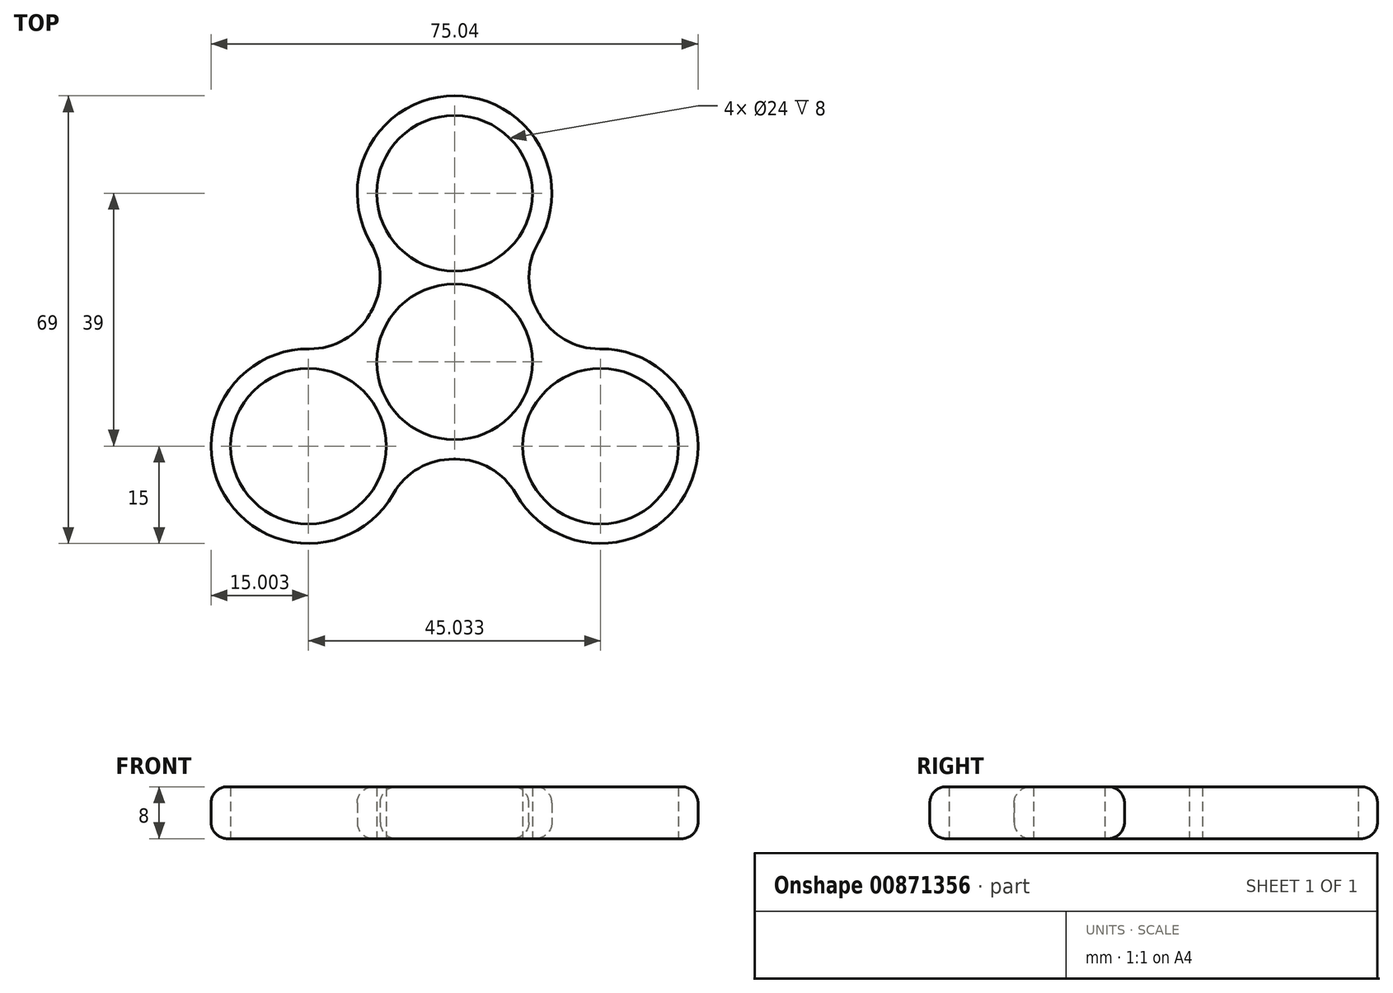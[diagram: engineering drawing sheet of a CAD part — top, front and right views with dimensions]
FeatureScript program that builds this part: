
annotation { "Feature Type Name" : "Feature", "Feature Type Description" : "" }
export const myFeature = defineFeature(function(context is Context, id is Id, definition is map)
    precondition{}
    {
        {
            var Q0;
            Q0=qCreatedBy(makeId("Top.planeOp"),FACE);
            var sketch = newSketch(context, id + "F0", { "sketchPlane" : qUnion([Q0])});
            skCircle(sketch, "E0", {"center": v(0, 0) * mm, "radius": 12 * mm});
            skCircle(sketch, "E1", {"center": v(0, 0) * mm, "radius": 26 * mm, "construction": true});
            skLineSegment(sketch, "E2", {"start": v(0, 0) * mm, "end": v(0, 26) * mm, "construction": true});
            skLineSegment(sketch, "E3", {"start": v(0, 0) * mm, "end": v(22.52, -13) * mm, "construction": true});
            skLineSegment(sketch, "E4", {"start": v(0, 0) * mm, "end": v(-22.52, -13) * mm, "construction": true});
            skCircle(sketch, "E5", {"center": v(0, 26) * mm, "radius": 12 * mm});
            skCircle(sketch, "E6", {"center": v(22.52, -13) * mm, "radius": 12 * mm});
            skCircle(sketch, "E7", {"center": v(-22.52, -13) * mm, "radius": 12 * mm});
            skCircle(sketch, "E8", {"center": v(0, 0) * mm, "radius": 41 * mm, "construction": true});
            skCircle(sketch, "E9", {"center": v(0, 26) * mm, "radius": 15 * mm});
            skCircle(sketch, "E10", {"center": v(-22.52, -13) * mm, "radius": 15 * mm});
            skCircle(sketch, "E11", {"center": v(22.52, -13) * mm, "radius": 15 * mm});
            skCircle(sketch, "E12", {"center": v(0, 0) * mm, "radius": 15 * mm});
            skSolve(sketch);
        }
        {
            var Q0;
            {var subQ0=sQuery(id+"F0.wireOp",EDGE,"E12");var subQ1=sQuery(id+"F0.wireOp",EDGE,"E5");var subQ2=makeQuery(id+"F0.imprint","INTERSECT",VERTEX,{"disambiguationData":[OD(0.0)],"derivedFrom":[subQ1,subQ0]});Q0=makeQuery(id+"F0.imprint","IMPRINT",FACE,{"disambiguationData":[TD([[makeQuery(id+"F0.imprint","IMPRINT",EDGE,{"disambiguationData":[TD([[subQ2,-1.0]])],"derivedFrom":subQ1}),-1.0]])]});}
            var Q1;
            {var subQ0=sQuery(id+"F0.wireOp",EDGE,"E9");var subQ1=sQuery(id+"F0.wireOp",EDGE,"E0");var subQ2=makeQuery(id+"F0.imprint","INTERSECT",VERTEX,{"disambiguationData":[OD(0.0)],"derivedFrom":[subQ1,subQ0]});Q1=makeQuery(id+"F0.imprint","IMPRINT",FACE,{"disambiguationData":[TD([[makeQuery(id+"F0.imprint","IMPRINT",EDGE,{"disambiguationData":[TD([[subQ2,-1.0]])],"derivedFrom":subQ1}),-1.0]])]});}
            var Q2;
            {var subQ0=sQuery(id+"F0.wireOp",EDGE,"E12");var subQ1=sQuery(id+"F0.wireOp",EDGE,"E7");var subQ2=makeQuery(id+"F0.imprint","INTERSECT",VERTEX,{"disambiguationData":[OD(0.0)],"derivedFrom":[subQ1,subQ0]});Q2=makeQuery(id+"F0.imprint","IMPRINT",FACE,{"disambiguationData":[TD([[makeQuery(id+"F0.imprint","IMPRINT",EDGE,{"disambiguationData":[TD([[subQ2,-1.0]])],"derivedFrom":subQ1}),-1.0]])]});}
            var Q3;
            {var subQ1=sQuery(id+"F0.wireOp",EDGE,"E10");var subQ3=sQuery(id+"F0.wireOp",EDGE,"E0");var subQ9=makeQuery(id+"F0.imprint","INTERSECT",VERTEX,{"disambiguationData":[OD(0.0)],"derivedFrom":[subQ3,subQ1]});Q3=makeQuery(id+"F0.imprint","IMPRINT",FACE,{"disambiguationData":[TD([[makeQuery(id+"F0.imprint","IMPRINT",EDGE,{"disambiguationData":[TD([[subQ9,-1.0]])],"derivedFrom":subQ3}),-1.0]])]});}
            var Q4;
            {var subQ1=sQuery(id+"F0.wireOp",EDGE,"E11");var subQ3=sQuery(id+"F0.wireOp",EDGE,"E0");var subQ4=makeQuery(id+"F0.imprint","INTERSECT",VERTEX,{"disambiguationData":[OD(0.0)],"derivedFrom":[subQ3,subQ1]});Q4=makeQuery(id+"F0.imprint","IMPRINT",FACE,{"disambiguationData":[TD([[makeQuery(id+"F0.imprint","IMPRINT",EDGE,{"disambiguationData":[TD([[subQ4,-1.0]])],"derivedFrom":subQ3}),-1.0]])]});}
            var Q5;
            {var subQ0=sQuery(id+"F0.wireOp",EDGE,"E10");var subQ1=sQuery(id+"F0.wireOp",EDGE,"E0");var subQ2=makeQuery(id+"F0.imprint","INTERSECT",VERTEX,{"disambiguationData":[OD(1.0)],"derivedFrom":[subQ1,subQ0]});Q5=makeQuery(id+"F0.imprint","IMPRINT",FACE,{"disambiguationData":[TD([[makeQuery(id+"F0.imprint","IMPRINT",EDGE,{"disambiguationData":[TD([[subQ2,-1.0]])],"derivedFrom":subQ1}),-1.0]])]});}
            var Q6;
            {var subQ0=sQuery(id+"F0.wireOp",EDGE,"E9");var subQ1=sQuery(id+"F0.wireOp",EDGE,"E0");var subQ2=makeQuery(id+"F0.imprint","INTERSECT",VERTEX,{"disambiguationData":[OD(1.0)],"derivedFrom":[subQ1,subQ0]});Q6=makeQuery(id+"F0.imprint","IMPRINT",FACE,{"disambiguationData":[TD([[makeQuery(id+"F0.imprint","IMPRINT",EDGE,{"disambiguationData":[TD([[subQ2,1.0]])],"derivedFrom":subQ1}),-1.0]])]});}
            var Q7;
            {var subQ1=sQuery(id+"F0.wireOp",EDGE,"E9");var subQ3=sQuery(id+"F0.wireOp",EDGE,"E0");var subQ8=makeQuery(id+"F0.imprint","INTERSECT",VERTEX,{"disambiguationData":[OD(0.0)],"derivedFrom":[subQ3,subQ1]});Q7=makeQuery(id+"F0.imprint","IMPRINT",FACE,{"disambiguationData":[TD([[makeQuery(id+"F0.imprint","IMPRINT",EDGE,{"disambiguationData":[TD([[subQ8,1.0]])],"derivedFrom":subQ3}),-1.0]])]});}
            var Q8;
            {var subQ0=sQuery(id+"F0.wireOp",EDGE,"E12");var subQ1=sQuery(id+"F0.wireOp",EDGE,"E6");var subQ2=makeQuery(id+"F0.imprint","INTERSECT",VERTEX,{"disambiguationData":[OD(0.0)],"derivedFrom":[subQ1,subQ0]});Q8=makeQuery(id+"F0.imprint","IMPRINT",FACE,{"disambiguationData":[TD([[makeQuery(id+"F0.imprint","IMPRINT",EDGE,{"disambiguationData":[TD([[subQ2,-1.0]])],"derivedFrom":subQ1}),-1.0]])]});}
            extrude(context, id + "F1", {"entities" : qUnion([Q0, Q1, Q2, Q3, Q4, Q5, Q6, Q7, Q8]), "depth" : 8 * mm, "offsetDistance" : 25 * mm});
        }
        {
            var Q0;
            {var subQ0=sQuery(id+"F0.wireOp",EDGE,"E12");var subQ1=sQuery(id+"F0.wireOp",EDGE,"E9");Q0=makeQuery(id+"F1.opExtrude","SWEPT_EDGE",EDGE,{"disambiguationData":[OSD([subQ1,subQ0]),TDD([makeQuery(id+"F0.imprint","INTERSECT",VERTEX,{"disambiguationData":[OD(1.0)],"derivedFrom":[subQ1,subQ0]})])]});}
            var Q1;
            {var subQ0=sQuery(id+"F0.wireOp",EDGE,"E12");var subQ1=sQuery(id+"F0.wireOp",EDGE,"E11");Q1=makeQuery(id+"F1.opExtrude","SWEPT_EDGE",EDGE,{"disambiguationData":[OSD([subQ1,subQ0]),TDD([makeQuery(id+"F0.imprint","INTERSECT",VERTEX,{"disambiguationData":[OD(0.0)],"derivedFrom":[subQ1,subQ0]})])]});}
            var Q2;
            {var subQ0=sQuery(id+"F0.wireOp",EDGE,"E12");var subQ1=sQuery(id+"F0.wireOp",EDGE,"E10");Q2=makeQuery(id+"F1.opExtrude","SWEPT_EDGE",EDGE,{"disambiguationData":[OSD([subQ1,subQ0]),TDD([makeQuery(id+"F0.imprint","INTERSECT",VERTEX,{"disambiguationData":[OD(0.0)],"derivedFrom":[subQ1,subQ0]})])]});}
            var Q3;
            {var subQ0=sQuery(id+"F0.wireOp",EDGE,"E12");var subQ1=sQuery(id+"F0.wireOp",EDGE,"E9");Q3=makeQuery(id+"F1.opExtrude","SWEPT_EDGE",EDGE,{"disambiguationData":[OSD([subQ1,subQ0]),TDD([makeQuery(id+"F0.imprint","INTERSECT",VERTEX,{"disambiguationData":[OD(0.0)],"derivedFrom":[subQ1,subQ0]})])]});}
            var Q4;
            {var subQ0=sQuery(id+"F0.wireOp",EDGE,"E12");var subQ1=sQuery(id+"F0.wireOp",EDGE,"E10");Q4=makeQuery(id+"F1.opExtrude","SWEPT_EDGE",EDGE,{"disambiguationData":[OSD([subQ1,subQ0]),TDD([makeQuery(id+"F0.imprint","INTERSECT",VERTEX,{"disambiguationData":[OD(1.0)],"derivedFrom":[subQ1,subQ0]})])]});}
            var Q5;
            {var subQ0=sQuery(id+"F0.wireOp",EDGE,"E12");var subQ1=sQuery(id+"F0.wireOp",EDGE,"E11");Q5=makeQuery(id+"F1.opExtrude","SWEPT_EDGE",EDGE,{"disambiguationData":[OSD([subQ1,subQ0]),TDD([makeQuery(id+"F0.imprint","INTERSECT",VERTEX,{"disambiguationData":[OD(1.0)],"derivedFrom":[subQ1,subQ0]})])]});}
            fillet(context, id + "F2", {"entities" : qUnion([Q0, Q1, Q2, Q3, Q4, Q5]), "radius" : 10.6 * mm, "tangentPropagation" : true, "allowEdgeOverflow" : false});
        }
        {
            var Q0;
            Q0=makeQuery(id+"F1.opExtrude","CAP_EDGE",EDGE,{"disambiguationData":[OSD([sQuery(id+"F0.wireOp",EDGE,"E10")])],"isStart":false});
            var Q1;
            Q1=makeQuery(id+"F1.opExtrude","CAP_EDGE",EDGE,{"disambiguationData":[OSD([sQuery(id+"F0.wireOp",EDGE,"E11")])],"isStart":false});
            var Q2;
            Q2=makeQuery(id+"F1.opExtrude","CAP_EDGE",EDGE,{"disambiguationData":[OSD([sQuery(id+"F0.wireOp",EDGE,"E9")])],"isStart":false});
            var Q3;
            Q3=makeQuery(id+"F1.opExtrude","CAP_EDGE",EDGE,{"disambiguationData":[OSD([sQuery(id+"F0.wireOp",EDGE,"E9")])],"isStart":true});
            var Q4;
            {var subQ0=sQuery(id+"F0.wireOp",EDGE,"E12");var subQ1=sQuery(id+"F0.wireOp",EDGE,"E9");Q4=makeQuery(id+"F2.opFillet","BLEND_EDGE",EDGE,{"blendedFrom":[makeQuery(id+"F1.opExtrude","SWEPT_EDGE",EDGE,{"disambiguationData":[OSD([subQ1,subQ0]),TDD([makeQuery(id+"F0.imprint","INTERSECT",VERTEX,{"disambiguationData":[OD(0.0)],"derivedFrom":[subQ1,subQ0]})])]}),makeQuery(id+"F1.opExtrude","CAP_FACE",FACE,{"disambiguationData":[OSD([sQuery(id+"F0.wireOp",EDGE,"E0"),sQuery(id+"F0.wireOp",EDGE,"E5"),sQuery(id+"F0.wireOp",EDGE,"E6"),sQuery(id+"F0.wireOp",EDGE,"E7"),subQ1,sQuery(id+"F0.wireOp",EDGE,"E10"),sQuery(id+"F0.wireOp",EDGE,"E11"),subQ0])],"isStart":true})],"blendedInto":[makeQuery(id+"F1.opExtrude","CAP_FACE",FACE,{"disambiguationData":[OSD([sQuery(id+"F0.wireOp",EDGE,"E0"),sQuery(id+"F0.wireOp",EDGE,"E5"),sQuery(id+"F0.wireOp",EDGE,"E6"),sQuery(id+"F0.wireOp",EDGE,"E7"),subQ1,sQuery(id+"F0.wireOp",EDGE,"E10"),sQuery(id+"F0.wireOp",EDGE,"E11"),subQ0])],"isStart":true})]});}
            var Q5;
            Q5=makeQuery(id+"F1.opExtrude","CAP_EDGE",EDGE,{"disambiguationData":[OSD([sQuery(id+"F0.wireOp",EDGE,"E10")])],"isStart":true});
            var Q6;
            Q6=makeQuery(id+"F1.opExtrude","CAP_EDGE",EDGE,{"disambiguationData":[OSD([sQuery(id+"F0.wireOp",EDGE,"E11")])],"isStart":true});
            fillet(context, id + "F3", {"entities" : qUnion([Q0, Q1, Q2, Q3, Q4, Q5, Q6]), "radius" : 2.5 * mm, "tangentPropagation" : true, "allowEdgeOverflow" : false});
        }
    });
